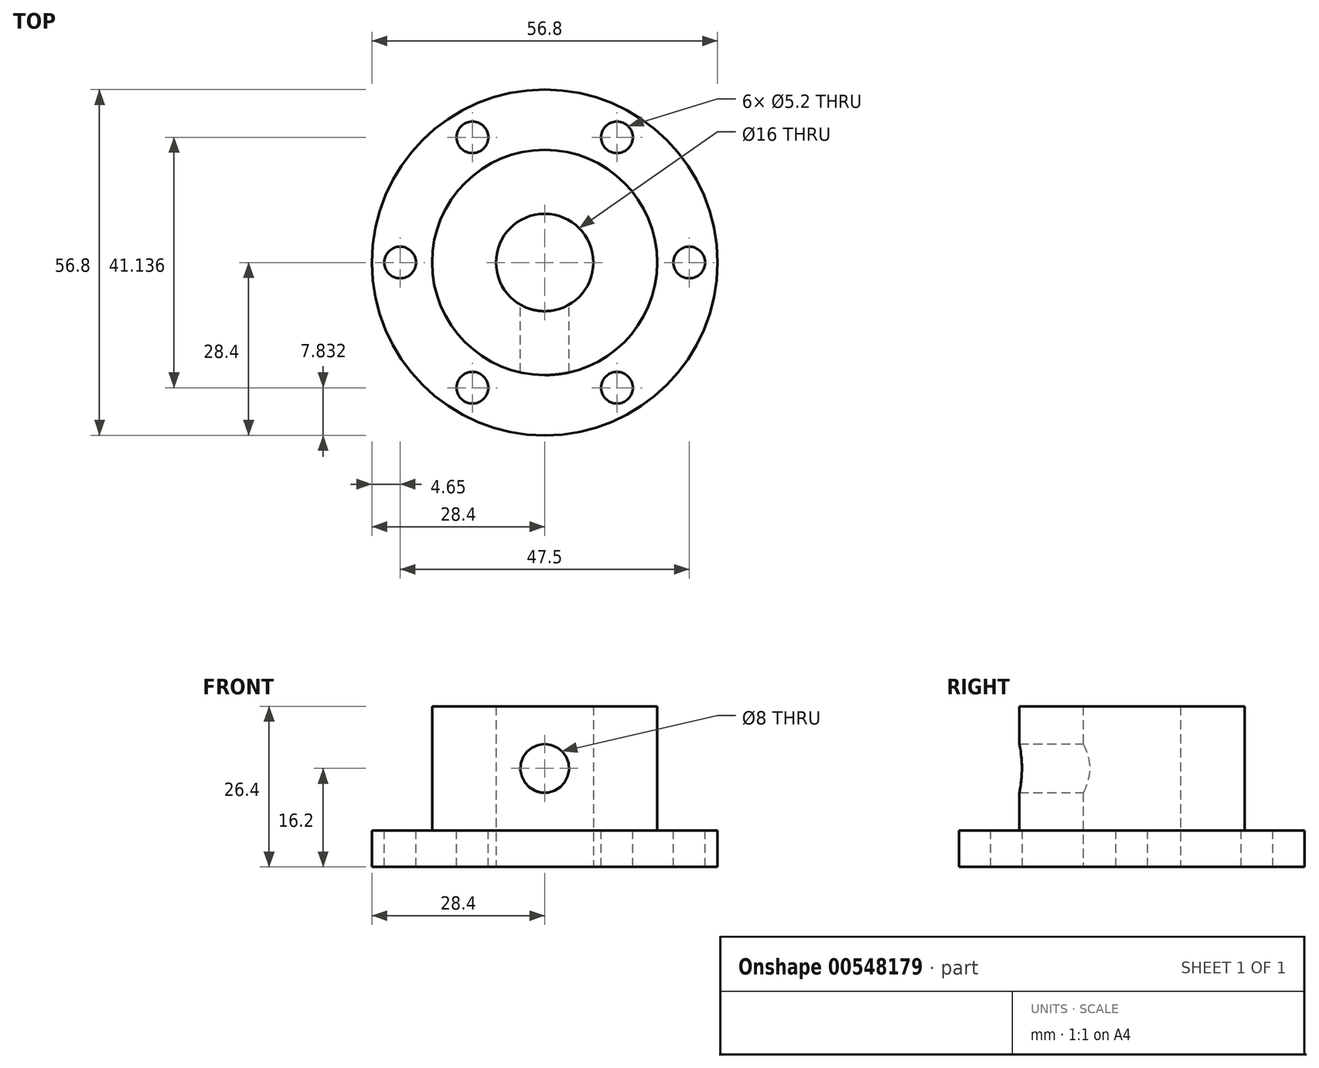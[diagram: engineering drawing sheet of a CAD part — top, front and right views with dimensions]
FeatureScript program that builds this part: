
annotation { "Feature Type Name" : "Feature", "Feature Type Description" : "" }
export const myFeature = defineFeature(function(context is Context, id is Id, definition is map)
    precondition{}
    {
        {
            var Q0;
            Q0=qCreatedBy(makeId("Front.planeOp"),FACE);
            var sketch = newSketch(context, id + "F0", { "sketchPlane" : qUnion([Q0])});
            skLineSegment(sketch, "E0", {"start": v(-8, 0) * mm, "end": v(-28.4, 0) * mm});
            skLineSegment(sketch, "E1", {"start": v(-28.4, 0) * mm, "end": v(-28.4, 6) * mm});
            skLineSegment(sketch, "E2", {"start": v(-28.4, 6) * mm, "end": v(-18.5, 6) * mm});
            skLineSegment(sketch, "E3", {"start": v(-18.5, 6) * mm, "end": v(-18.5, 26.4) * mm});
            skLineSegment(sketch, "E4", {"start": v(-18.5, 26.4) * mm, "end": v(-8, 26.4) * mm});
            skLineSegment(sketch, "E5", {"start": v(-8, 26.4) * mm, "end": v(-8, 0) * mm});
            skLineSegment(sketch, "E6", {"start": v(0, 0) * mm, "end": v(0, 43.03) * mm, "construction": true});
            skSolve(sketch);
        }
        {
            var Q0;
            Q0 = qSketchRegion(id + "F0", true);
            var Q1;
            Q1=sQuery(id+"F0.wireOp",EDGE,"E6");
            revolve(context, id + "F1", {"entities" : qUnion([Q0]), "axis" : qUnion([Q1]), "revolveType" : RevolveType.FULL});
        }
        {
            var Q0;
            Q0=makeQuery(id+"F1.opRevolve","SWEPT_FACE",FACE,{"disambiguationData":[OSD([sQuery(id+"F0.wireOp",EDGE,"E2")])]});
            var sketch = newSketch(context, id + "F2", { "sketchPlane" : qUnion([Q0])});
            skCircle(sketch, "E7", {"center": v(0, 0) * mm, "radius": 23.75 * mm, "construction": true});
            skCircle(sketch, "E8", {"center": v(-23.75, 0) * mm, "radius": 2.6 * mm});
            skCircle(sketch, "E9.1.0", {"center": v(-11.88, -20.57) * mm, "radius": 2.6 * mm});
            skCircle(sketch, "E9.2.0", {"center": v(11.87, -20.57) * mm, "radius": 2.6 * mm});
            skCircle(sketch, "E9.3.0", {"center": v(23.75, 0) * mm, "radius": 2.6 * mm});
            skCircle(sketch, "E9.4.0", {"center": v(11.88, 20.57) * mm, "radius": 2.6 * mm});
            skCircle(sketch, "E9.5.0", {"center": v(-11.88, 20.57) * mm, "radius": 2.6 * mm});
            skSolve(sketch);
        }
        {
            var Q0;
            Q0 = qSketchRegion(id + "F2", true);
            extrude(context, id + "F3", {"entities" : qUnion([Q0]), "operationType" : NewBodyOperationType.REMOVE, "endBound" : BoundingType.THROUGH_ALL, "oppositeDirection" : true, "depth" : 25 * mm, "offsetDistance" : 25 * mm});
        }
        {
            var Q0;
            Q0=qCreatedBy(makeId("Front.planeOp"),FACE);
            var sketch = newSketch(context, id + "F4", { "sketchPlane" : qUnion([Q0])});
            skLineSegment(sketch, "E10", {"start": v(0, 0) * mm, "end": v(0, 16.2) * mm, "construction": true});
            skCircle(sketch, "E11", {"center": v(0, 16.2) * mm, "radius": 4 * mm});
            skSolve(sketch);
        }
        {
            var Q0;
            Q0 = qSketchRegion(id + "F4", true);
            extrude(context, id + "F5", {"entities" : qUnion([Q0]), "operationType" : NewBodyOperationType.REMOVE, "depth" : 25 * mm, "offsetDistance" : 25 * mm});
        }
    });
